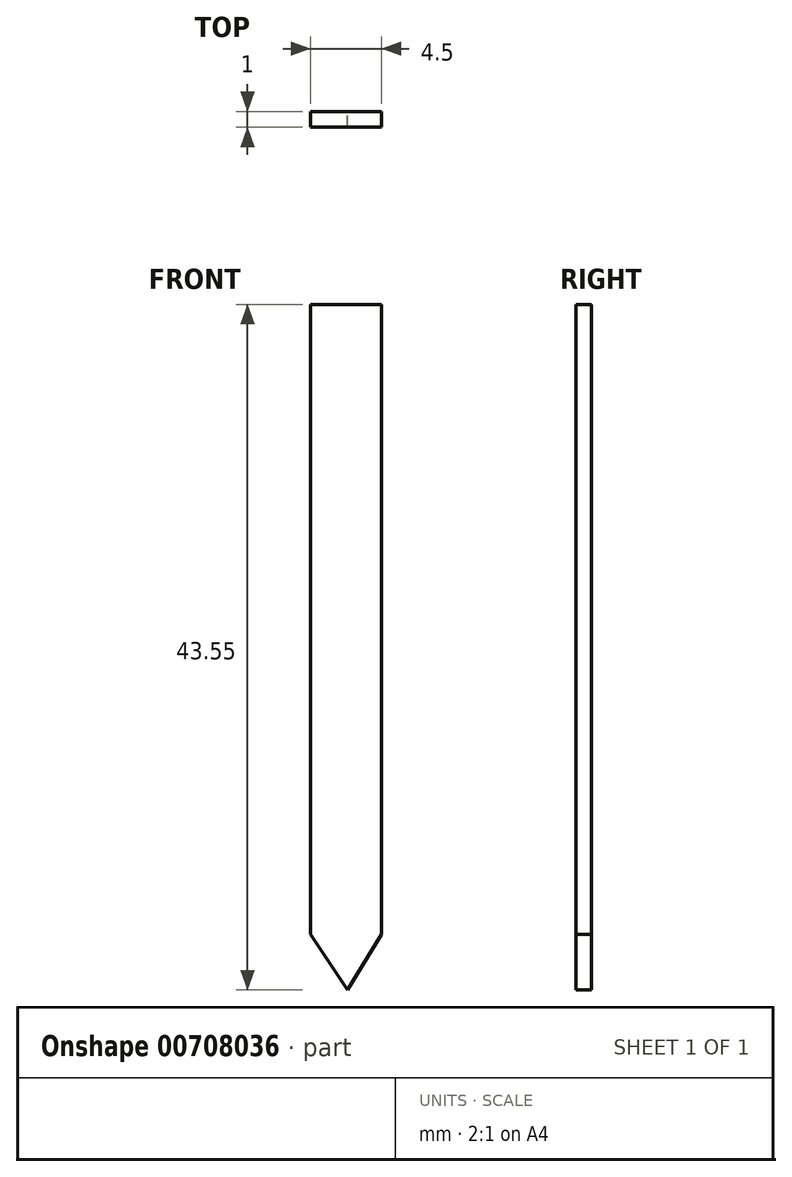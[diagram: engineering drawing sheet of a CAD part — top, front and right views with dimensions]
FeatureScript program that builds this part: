
annotation { "Feature Type Name" : "Feature", "Feature Type Description" : "" }
export const myFeature = defineFeature(function(context is Context, id is Id, definition is map)
    precondition{}
    {
        {
            var Q0;
            Q0=qCreatedBy(makeId("Front.planeOp"),FACE);
            var sketch = newSketch(context, id + "F0", { "sketchPlane" : qUnion([Q0])});
            skLineSegment(sketch, "E0.bottom", {"start": v(-5.9, 40) * mm, "end": v(-1.4, 40) * mm});
            skLineSegment(sketch, "E0.left", {"start": v(-5.9, 40) * mm, "end": v(-5.9, 0) * mm});
            skLineSegment(sketch, "E0.right", {"start": v(-1.4, 40) * mm, "end": v(-1.4, 0) * mm});
            skLineSegment(sketch, "E1", {"start": v(-5.9, 0) * mm, "end": v(-3.55, -3.55) * mm});
            skLineSegment(sketch, "E2", {"start": v(-3.55, -3.55) * mm, "end": v(-1.4, 0) * mm});
            skSolve(sketch);
        }
        {
            var Q0;
            Q0=makeQuery(id+"F0.imprint","IMPRINT",FACE,{"disambiguationData":[TD([[makeQuery(id+"F0.imprint","IMPRINT",EDGE,{"derivedFrom":sQuery(id+"F0.wireOp",EDGE,"E0.bottom")}),-1.0]])]});
            extrude(context, id + "F1", {"entities" : qUnion([Q0]), "depth" : 1 * mm, "offsetDistance" : 25 * mm});
        }
    });
